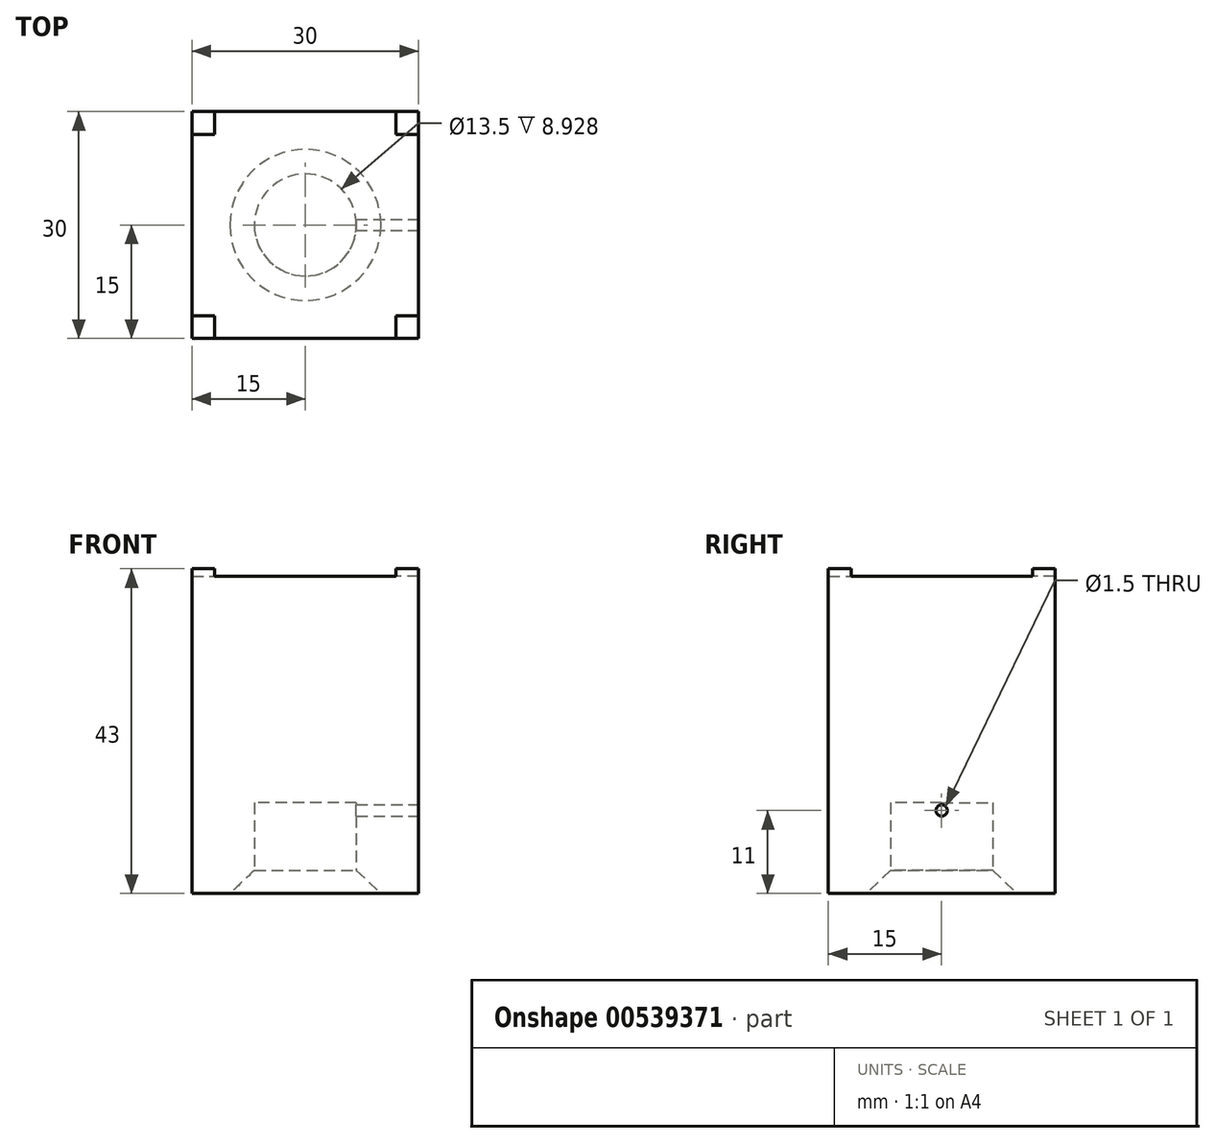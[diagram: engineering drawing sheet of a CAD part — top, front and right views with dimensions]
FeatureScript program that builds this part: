
annotation { "Feature Type Name" : "Feature", "Feature Type Description" : "" }
export const myFeature = defineFeature(function(context is Context, id is Id, definition is map)
    precondition{}
    {
        {
            var Q0;
            Q0=qCreatedBy(makeId("Top.planeOp"),FACE);
            var sketch = newSketch(context, id + "F0", { "sketchPlane" : qUnion([Q0])});
            skLineSegment(sketch, "E0.bottom", {"start": v(-15, 15) * mm, "end": v(15, 15) * mm});
            skLineSegment(sketch, "E0.top", {"start": v(-15, -15) * mm, "end": v(15, -15) * mm});
            skLineSegment(sketch, "E0.left", {"start": v(-15, 15) * mm, "end": v(-15, -15) * mm});
            skLineSegment(sketch, "E0.right", {"start": v(15, 15) * mm, "end": v(15, -15) * mm});
            skSolve(sketch);
        }
        {
            var Q0;
            Q0=qSketchRegion(id+"F0",true);
            extrude(context, id + "F1", {"entities" : qUnion([Q0]), "depth" : 42 * mm, "offsetDistance" : 25 * mm});
        }
        {
            var Q0;
            Q0=qCreatedBy(makeId("Top.planeOp"),FACE);
            var sketch = newSketch(context, id + "F2", { "sketchPlane" : qUnion([Q0])});
            skCircle(sketch, "E1", {"center": v(0, 0) * mm, "radius": 6.75 * mm});
            skSolve(sketch);
        }
        {
            var Q0;
            Q0=qSketchRegion(id+"F2",true);
            extrude(context, id + "F3", {"entities" : qUnion([Q0]), "operationType" : NewBodyOperationType.REMOVE, "depth" : 12 * mm, "offsetDistance" : 25 * mm});
        }
        {
            var Q0;
            Q0=qCreatedBy(makeId("Front.planeOp"),FACE);
            var sketch = newSketch(context, id + "F4", { "sketchPlane" : qUnion([Q0])});
            skLineSegment(sketch, "E2", {"start": v(0, 0) * mm, "end": v(0, 9.45) * mm});
            skLineSegment(sketch, "E3", {"start": v(0, 9.45) * mm, "end": v(10, 0) * mm});
            skLineSegment(sketch, "E4", {"start": v(10, 0) * mm, "end": v(-10, 0) * mm});
            skLineSegment(sketch, "E5", {"start": v(0, 9.45) * mm, "end": v(0, 0) * mm});
            skLineSegment(sketch, "E6", {"start": v(10, 0) * mm, "end": v(0, 0) * mm});
            skSolve(sketch);
        }
        {
            var Q0;
            Q0=qSketchRegion(id+"F4",true);
            var Q1;
            Q1=sQuery(id+"F4.wireOp",EDGE,"E5");
            revolve(context, id + "F5", {"operationType" : NewBodyOperationType.REMOVE, "entities" : qUnion([Q0]), "axis" : qUnion([Q1]), "revolveType" : RevolveType.FULL});
        }
        {
            var Q0;
            Q0=makeQuery(id+"F1.opExtrude","CAP_FACE",FACE,{"disambiguationData":[OSD([sQuery(id+"F0.wireOp",EDGE,"E0.bottom"),sQuery(id+"F0.wireOp",EDGE,"E0.top"),sQuery(id+"F0.wireOp",EDGE,"E0.left"),sQuery(id+"F0.wireOp",EDGE,"E0.right")])],"isStart":false});
            var sketch = newSketch(context, id + "F6", { "sketchPlane" : qUnion([Q0])});
            skLineSegment(sketch, "E7.bottom", {"start": v(-15, 15) * mm, "end": v(-12, 15) * mm});
            skLineSegment(sketch, "E7.top", {"start": v(-15, 12) * mm, "end": v(-12, 12) * mm});
            skLineSegment(sketch, "E7.left", {"start": v(-15, 15) * mm, "end": v(-15, 12) * mm});
            skLineSegment(sketch, "E7.right", {"start": v(-12, 15) * mm, "end": v(-12, 12) * mm});
            skLineSegment(sketch, "E8.bottom", {"start": v(15, 15) * mm, "end": v(12, 15) * mm});
            skLineSegment(sketch, "E8.top", {"start": v(15, 12) * mm, "end": v(12, 12) * mm});
            skLineSegment(sketch, "E8.left", {"start": v(15, 15) * mm, "end": v(15, 12) * mm});
            skLineSegment(sketch, "E8.right", {"start": v(12, 15) * mm, "end": v(12, 12) * mm});
            skLineSegment(sketch, "E9.bottom", {"start": v(15, -15) * mm, "end": v(12, -15) * mm});
            skLineSegment(sketch, "E9.top", {"start": v(15, -12) * mm, "end": v(12, -12) * mm});
            skLineSegment(sketch, "E9.left", {"start": v(15, -15) * mm, "end": v(15, -12) * mm});
            skLineSegment(sketch, "E9.right", {"start": v(12, -15) * mm, "end": v(12, -12) * mm});
            skLineSegment(sketch, "E10.bottom", {"start": v(-15, -15) * mm, "end": v(-12, -15) * mm});
            skLineSegment(sketch, "E10.top", {"start": v(-15, -12) * mm, "end": v(-12, -12) * mm});
            skLineSegment(sketch, "E10.left", {"start": v(-15, -15) * mm, "end": v(-15, -12) * mm});
            skLineSegment(sketch, "E10.right", {"start": v(-12, -15) * mm, "end": v(-12, -12) * mm});
            skSolve(sketch);
        }
        {
            var Q0;
            Q0 = qSketchRegion(id + "F6", true);
            extrude(context, id + "F7", {"entities" : qUnion([Q0]), "operationType" : NewBodyOperationType.ADD, "depth" : 1 * mm, "offsetDistance" : 25 * mm});
        }
        {
            var Q0;
            Q0=makeQuery(id+"F7.boolean.opBoolean","MERGE",FACE,{"derivedFrom":[makeQuery(id+"F1.opExtrude","SWEPT_FACE",FACE,{"disambiguationData":[OSD([sQuery(id+"F0.wireOp",EDGE,"E0.right")])]}),makeQuery(id+"F7.opExtrude","SWEPT_FACE",FACE,{"disambiguationData":[OSD([sQuery(id+"F6.wireOp",EDGE,"E8.left")])]}),makeQuery(id+"F7.opExtrude","SWEPT_FACE",FACE,{"disambiguationData":[OSD([sQuery(id+"F6.wireOp",EDGE,"E9.left")])]})]});
            var sketch = newSketch(context, id + "F8", { "sketchPlane" : qUnion([Q0])});
            skCircle(sketch, "E11", {"center": v(0, 11) * mm, "radius": 0.75 * mm});
            skSolve(sketch);
        }
        {
            var Q0;
            Q0 = qSketchRegion(id + "F8", true);
            extrude(context, id + "F9", {"entities" : qUnion([Q0]), "operationType" : NewBodyOperationType.REMOVE, "endBound" : BoundingType.UP_TO_NEXT, "oppositeDirection" : true, "depth" : 25 * mm, "offsetDistance" : 25 * mm});
        }
    });
